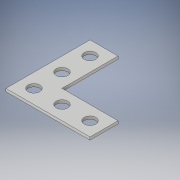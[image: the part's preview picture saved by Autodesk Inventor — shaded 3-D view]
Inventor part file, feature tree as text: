
AUTODESK INVENTOR PART (.ipt)
format: ipt  version: 2018 (Build 220112000, 112)  size: 125,952 bytes
history: native  units: in
note: dims shown in document units (in); Inventor stores cm internally (conversion verified against a paired STEP export)
features: extrude x1, sketch x1
ambient origin geometry x8: Origin, YZ Plane, XZ Plane, XY Plane, X Axis, Y Axis, Z Axis, Center Point
bodies: Solid1 (feature_tree)
feature tree (2):
  extrude  "Extrusion1"  Depth=1.0in
  sketch  "Sketch1"  dims[d0=0.0in d1=1.0in d2=3.0in d3=2.0in d4=1.0in d5=0.5in d6=0.5in d7=0.5in d8=0.5in d9=1.0in d10=1.0in d11=0.4167in d12=0.4167in d13=0.4167in d14=0.4167in d15=0.4167in d16=0.5in d17=0.5in d18=0.5in d19=1.0in d20=0.5in d21=0.1in d22=0.0in]
